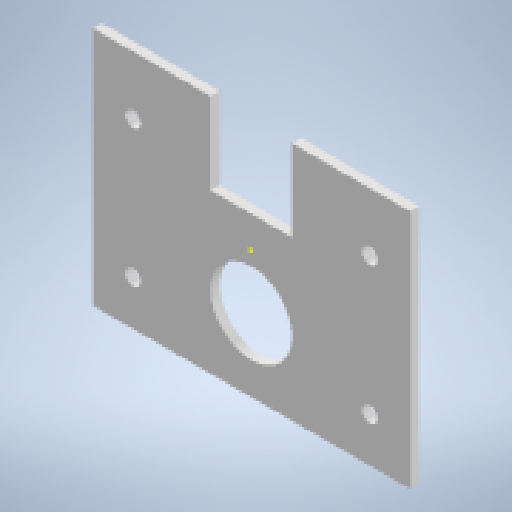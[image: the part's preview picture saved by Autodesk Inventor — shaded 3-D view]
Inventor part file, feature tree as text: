
AUTODESK INVENTOR PART (.ipt)
format: ipt  version: 2025.1 (Build 291241000, 241)  size: 152,576 bytes
history: native  units: in
note: dims shown in document units (in); Inventor stores cm internally (conversion verified against a paired STEP export)
features: sketch x3, extrude x1, hole x1, mirror x1
ambient origin geometry x8: Origin, YZ Plane, XZ Plane, XY Plane, X Axis, Y Axis, Z Axis, Center Point
bodies: Solid1 (feature_tree)
feature tree (6):
  extrude  "Extrusion1"  Depth=3.455in
  hole  "Hole1"  [1 undecoded]
  mirror  "Mirror1"
  sketch  "Sketch3"  dims[d4=1.01in d5=1.125in d6=0.125in d7=0.0in d8=0.217in d9=0.75in d10=0.409in d11=0.25in d12=90.0deg d13=1.0in d14=0.8108in d15=1.9in d16=0.56in d17=0.56in d18=0.62in]
  sketch  "Sketch1"  dims[d0=4.4in d1=3.455in]
  sketch  "Sketch2"  dims[d2=1.13in d3=1.13in]
note: 1 required parameter value undecoded (feature->parameter linkage not recoverable at this tier; creation-order binding heuristic only, values carry confidence <= 0.55)
